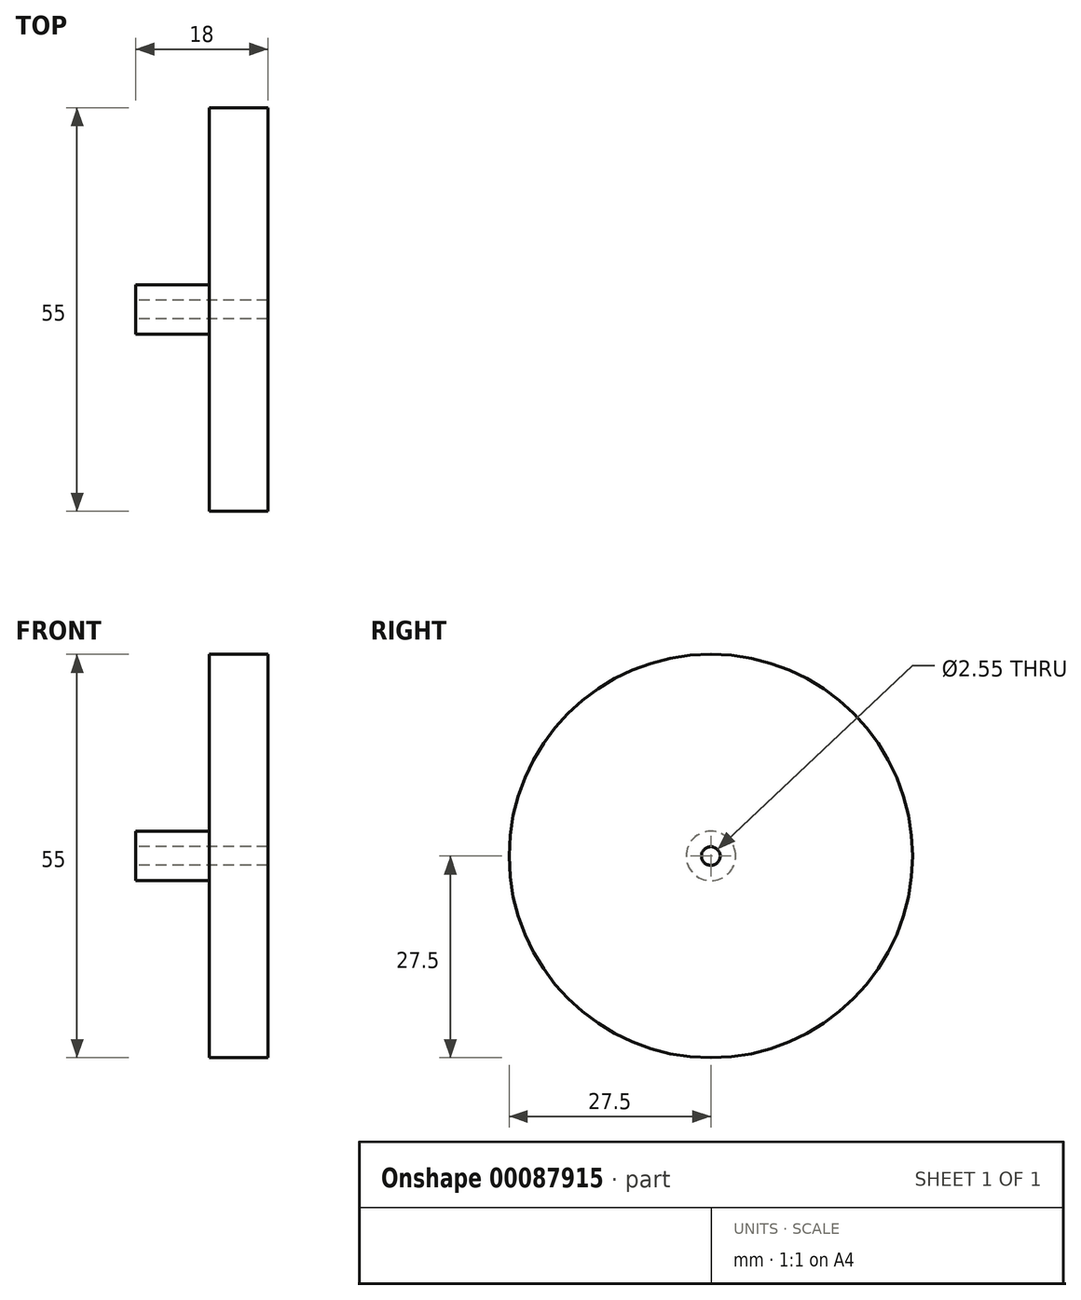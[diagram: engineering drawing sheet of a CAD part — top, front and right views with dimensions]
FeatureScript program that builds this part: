
annotation { "Feature Type Name" : "Feature", "Feature Type Description" : "" }
export const myFeature = defineFeature(function(context is Context, id is Id, definition is map)
    precondition{}
    {
        {
            var Q0;
            Q0=qCreatedBy(makeId("Right.planeOp"),FACE);
            var sketch = newSketch(context, id + "F0", { "sketchPlane" : qUnion([Q0])});
            skCircle(sketch, "E0", {"center": v(0, 0) * mm, "radius": 3.38 * mm});
            skSolve(sketch);
        }
        {
            var Q0;
            Q0 = qSketchRegion(id + "F0", true);
            extrude(context, id + "F1", {"entities" : qUnion([Q0]), "depth" : 10 * mm});
        }
        {
            var Q0;
            Q0=makeQuery(id+"F1.opExtrude","CAP_FACE",FACE,{"disambiguationData":[OSD([sQuery(id+"F0.wireOp",EDGE,"E0")])],"isStart":false});
            var sketch = newSketch(context, id + "F2", { "sketchPlane" : qUnion([Q0])});
            skCircle(sketch, "E1", {"center": v(0, 0) * mm, "radius": 27.5 * mm});
            skSolve(sketch);
        }
        {
            var Q0;
            Q0=makeQuery(id+"F2.imprint","IMPRINT",FACE,{"disambiguationData":[TD([[makeQuery(id+"F2.imprint","IMPRINT",EDGE,{"derivedFrom":sQuery(id+"F2.wireOp",EDGE,"E1")}),1.0]])]});
            var Q1;
            Q1=makeQuery(id+"F2.imprint","IMPRINT",FACE,{"disambiguationData":[TD([[makeQuery(id+"F2.imprint","IMPRINT",EDGE,{"derivedFrom":makeQuery(id+"F1.opExtrude","CAP_EDGE",EDGE,{"disambiguationData":[OSD([sQuery(id+"F0.wireOp",EDGE,"E0")])],"isStart":false})}),1.0]])]});
            extrude(context, id + "F3", {"entities" : qUnion([Q0, Q1]), "operationType" : NewBodyOperationType.ADD, "depth" : 8 * mm});
        }
        {
            var Q0;
            Q0=makeQuery(id+"F1.opExtrude","CAP_FACE",FACE,{"disambiguationData":[OSD([sQuery(id+"F0.wireOp",EDGE,"E0")])],"isStart":true});
            var sketch = newSketch(context, id + "F4", { "sketchPlane" : qUnion([Q0])});
            skCircle(sketch, "E2", {"center": v(0, 0) * mm, "radius": 1.27 * mm});
            skSolve(sketch);
        }
        {
            var Q0;
            Q0 = qSketchRegion(id + "F4", true);
            extrude(context, id + "F5", {"entities" : qUnion([Q0]), "operationType" : NewBodyOperationType.REMOVE, "oppositeDirection" : true, "depth" : 25.4 * mm});
        }
    });
